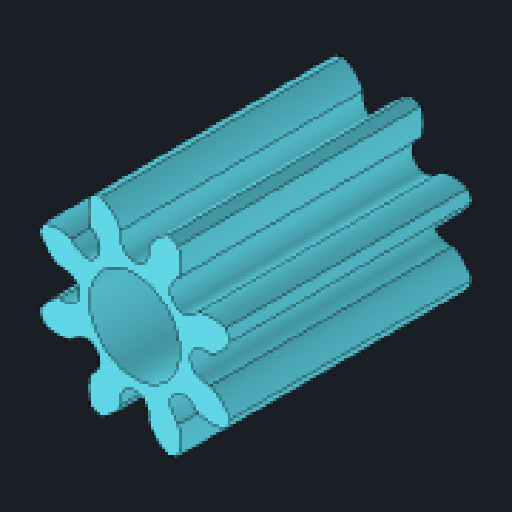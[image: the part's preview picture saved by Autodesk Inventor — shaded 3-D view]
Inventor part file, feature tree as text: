
AUTODESK INVENTOR PART (.ipt)
format: ipt  version: 2023.2 (Build 272271030, 271C)  size: 484,352 bytes
history: native  units: mm
features: sketch x3, extrude x3, pattern_circular x1, hole x1
ambient origin geometry x8: Origin, YZ Plane, XZ Plane, XY Plane, X Axis, Y Axis, Z Axis, Center Point
bodies: Solid1 (feature_tree)
feature tree (8):
  sketch  "Sketch1"  dims[d0=12.0mm d1=0.0mm d2=0.0mm d3=0.0mm]
  extrude  "Extrusion1"  TaperAngle=0.0deg  [1 undecoded]
  extrude  "Extrusion2"  Depth=4.0mm TaperAngle=0.0deg
  pattern_circular  "Circular Pattern1"  [2 undecoded]
  hole  "Hole1"  [1 undecoded]
  extrude  "Extrusion4"  [1 undecoded]
  sketch  "Sketch2"  dims[d4=80.0mm d5=360.0deg]
  sketch  "Sketch4"  dims[d7=2.5mm d8=6.0mm d9=4.5mm d10=5.8mm d11=90.0deg d12=8.0mm d13=20.594885mm d17=4.0mm d18=0.0mm d19=0.0mm d20=0.0mm]
note: 5 required parameter values undecoded (feature->parameter linkage not recoverable at this tier; creation-order binding heuristic only, values carry confidence <= 0.55)
